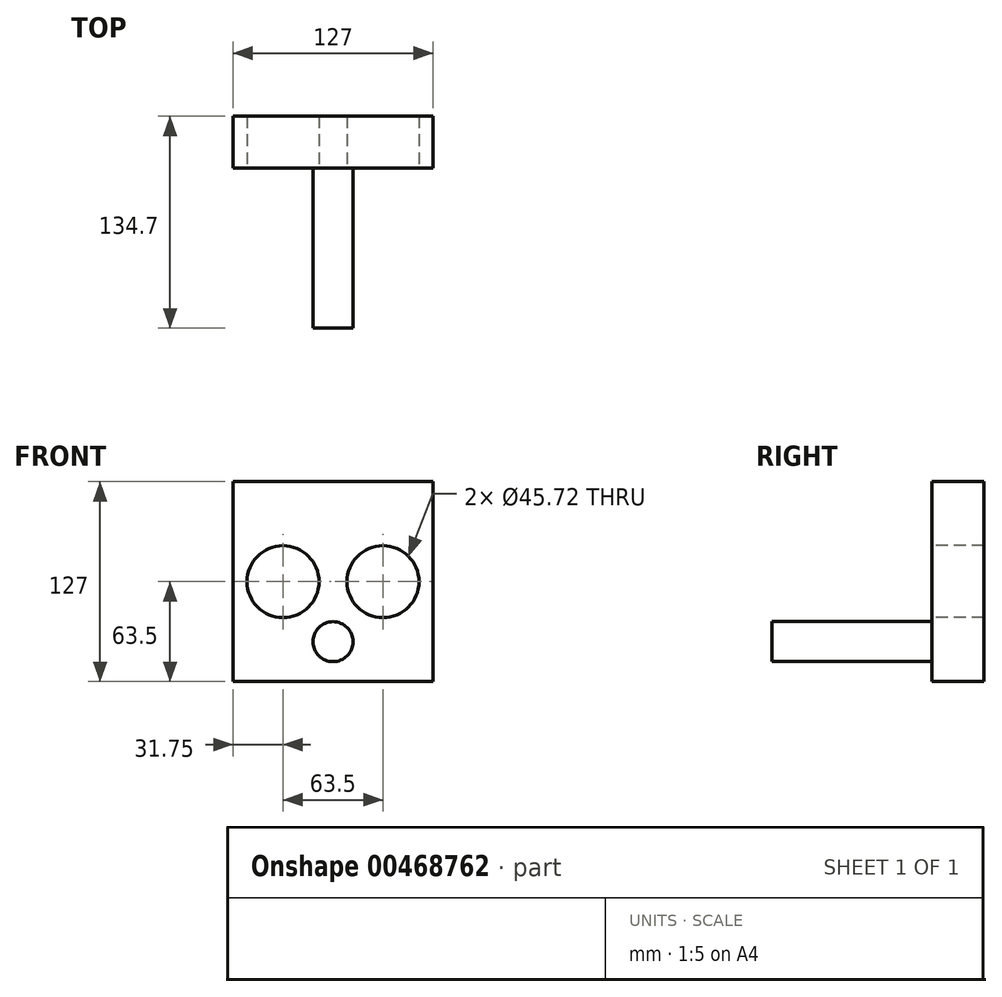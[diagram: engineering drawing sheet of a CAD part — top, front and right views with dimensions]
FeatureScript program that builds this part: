
annotation { "Feature Type Name" : "Feature", "Feature Type Description" : "" }
export const myFeature = defineFeature(function(context is Context, id is Id, definition is map)
    precondition{}
    {
        {
            var Q0;
            Q0=qCreatedBy(makeId("Front.planeOp"),FACE);
            var sketch = newSketch(context, id + "F0", { "sketchPlane" : qUnion([Q0])});
            skLineSegment(sketch, "E0.bottom", {"start": v(63.5, -63.5) * mm, "end": v(-63.5, -63.5) * mm});
            skLineSegment(sketch, "E0.top", {"start": v(63.5, 63.5) * mm, "end": v(-63.5, 63.5) * mm});
            skLineSegment(sketch, "E0.left", {"start": v(63.5, -63.5) * mm, "end": v(63.5, 63.5) * mm});
            skLineSegment(sketch, "E0.right", {"start": v(-63.5, -63.5) * mm, "end": v(-63.5, 63.5) * mm});
            skPoint(sketch, "E0.middle", {"position": v(0, 0) * mm});
            skCircle(sketch, "E1", {"center": v(-31.75, 0) * mm, "radius": 22.86 * mm});
            skCircle(sketch, "E2", {"center": v(31.75, 0) * mm, "radius": 22.86 * mm});
            skSolve(sketch);
        }
        {
            var Q0;
            Q0=makeQuery(id+"F0.imprint","IMPRINT",FACE,{"disambiguationData":[TD([[makeQuery(id+"F0.imprint","IMPRINT",EDGE,{"derivedFrom":sQuery(id+"F0.wireOp",EDGE,"E0.bottom")}),-1.0]])]});
            extrude(context, id + "F1", {"entities" : qUnion([Q0]), "oppositeDirection" : true, "depth" : 33.1 * mm});
        }
        {
            var Q0;
            Q0=makeQuery(id+"F1.opExtrude","CAP_FACE",FACE,{"disambiguationData":[OSD([sQuery(id+"F0.wireOp",EDGE,"E0.bottom"),sQuery(id+"F0.wireOp",EDGE,"E0.top"),sQuery(id+"F0.wireOp",EDGE,"E0.left"),sQuery(id+"F0.wireOp",EDGE,"E0.right"),sQuery(id+"F0.wireOp",EDGE,"E1"),sQuery(id+"F0.wireOp",EDGE,"E2")])],"isStart":true});
            var sketch = newSketch(context, id + "F2", { "sketchPlane" : qUnion([Q0])});
            skCircle(sketch, "E3", {"center": v(0, -38.1) * mm, "radius": 12.7 * mm});
            skSolve(sketch);
        }
        {
            var Q0;
            Q0 = qSketchRegion(id + "F2", true);
            extrude(context, id + "F3", {"entities" : qUnion([Q0]), "operationType" : NewBodyOperationType.ADD, "depth" : 101.6 * mm});
        }
    });
